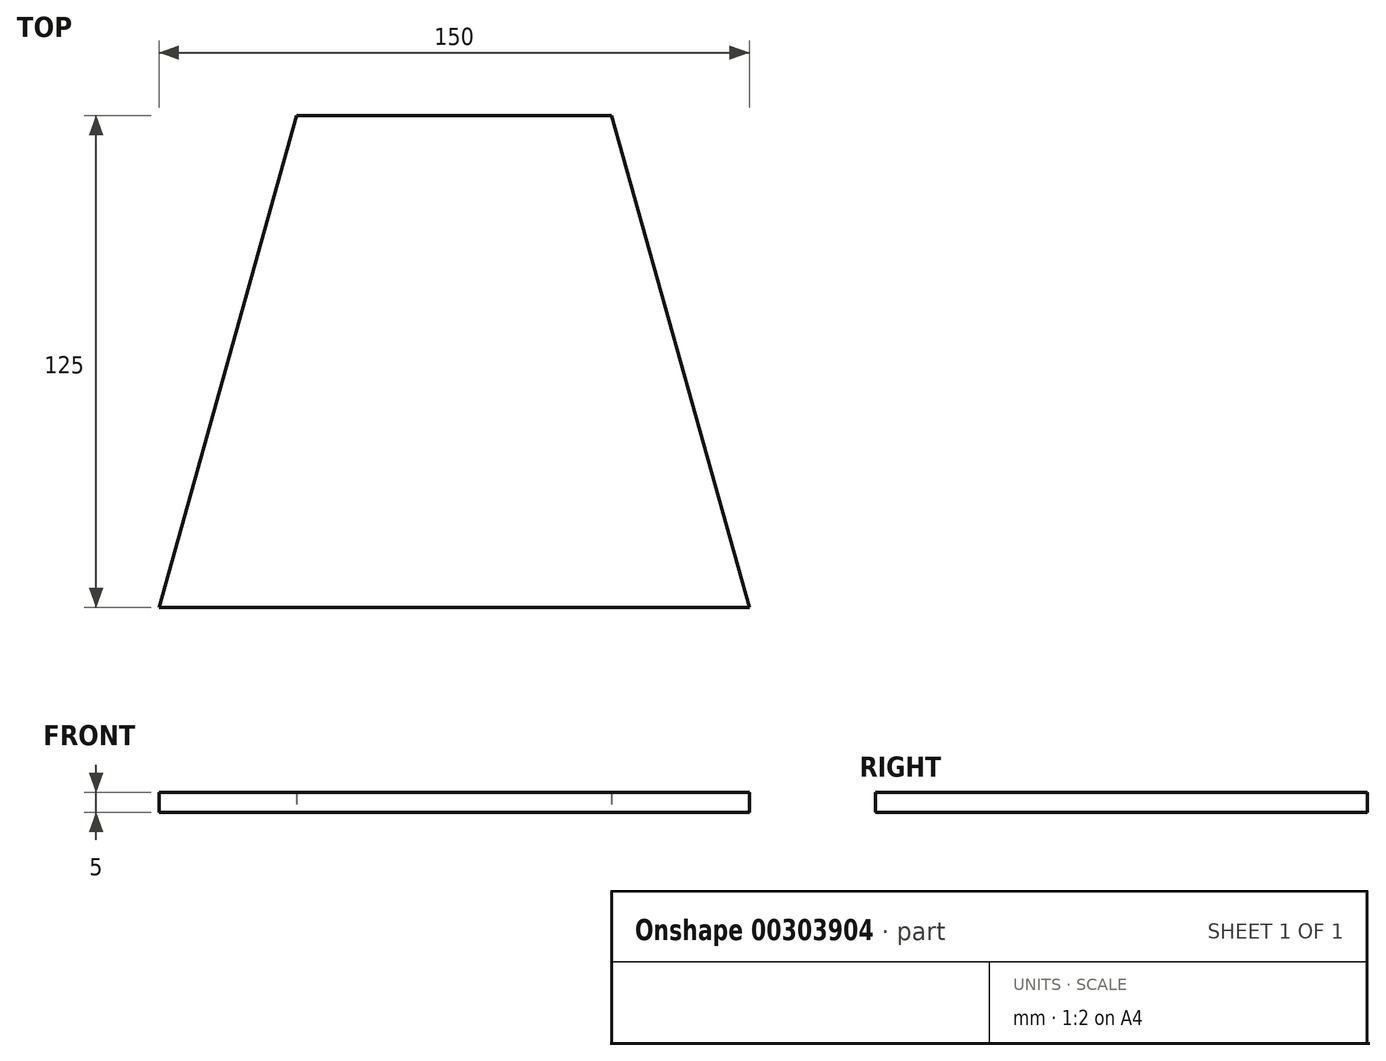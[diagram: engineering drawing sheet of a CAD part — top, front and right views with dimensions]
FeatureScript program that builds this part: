
annotation { "Feature Type Name" : "Feature", "Feature Type Description" : "" }
export const myFeature = defineFeature(function(context is Context, id is Id, definition is map)
    precondition{}
    {
        {
            var Q0;
            Q0=qCreatedBy(makeId("Top.planeOp"),FACE);
            var sketch = newSketch(context, id + "F0", { "sketchPlane" : qUnion([Q0])});
            skLineSegment(sketch, "E0", {"start": v(-92.66, 125) * mm, "end": v(-12.66, 125) * mm});
            skLineSegment(sketch, "E1", {"start": v(-12.66, 125) * mm, "end": v(22.34, 0) * mm});
            skLineSegment(sketch, "E2", {"start": v(22.34, 0) * mm, "end": v(-127.66, 0) * mm});
            skLineSegment(sketch, "E3", {"start": v(-127.66, 0) * mm, "end": v(-92.66, 125) * mm});
            skSolve(sketch);
        }
        {
            var Q0;
            Q0=makeQuery(id+"F0.imprint","IMPRINT",FACE,{"disambiguationData":[TD([[makeQuery(id+"F0.imprint","IMPRINT",EDGE,{"derivedFrom":sQuery(id+"F0.wireOp",EDGE,"E0")}),-1.0]])]});
            extrude(context, id + "F1", {"entities" : qUnion([Q0]), "depth" : 5 * mm});
        }
    });
